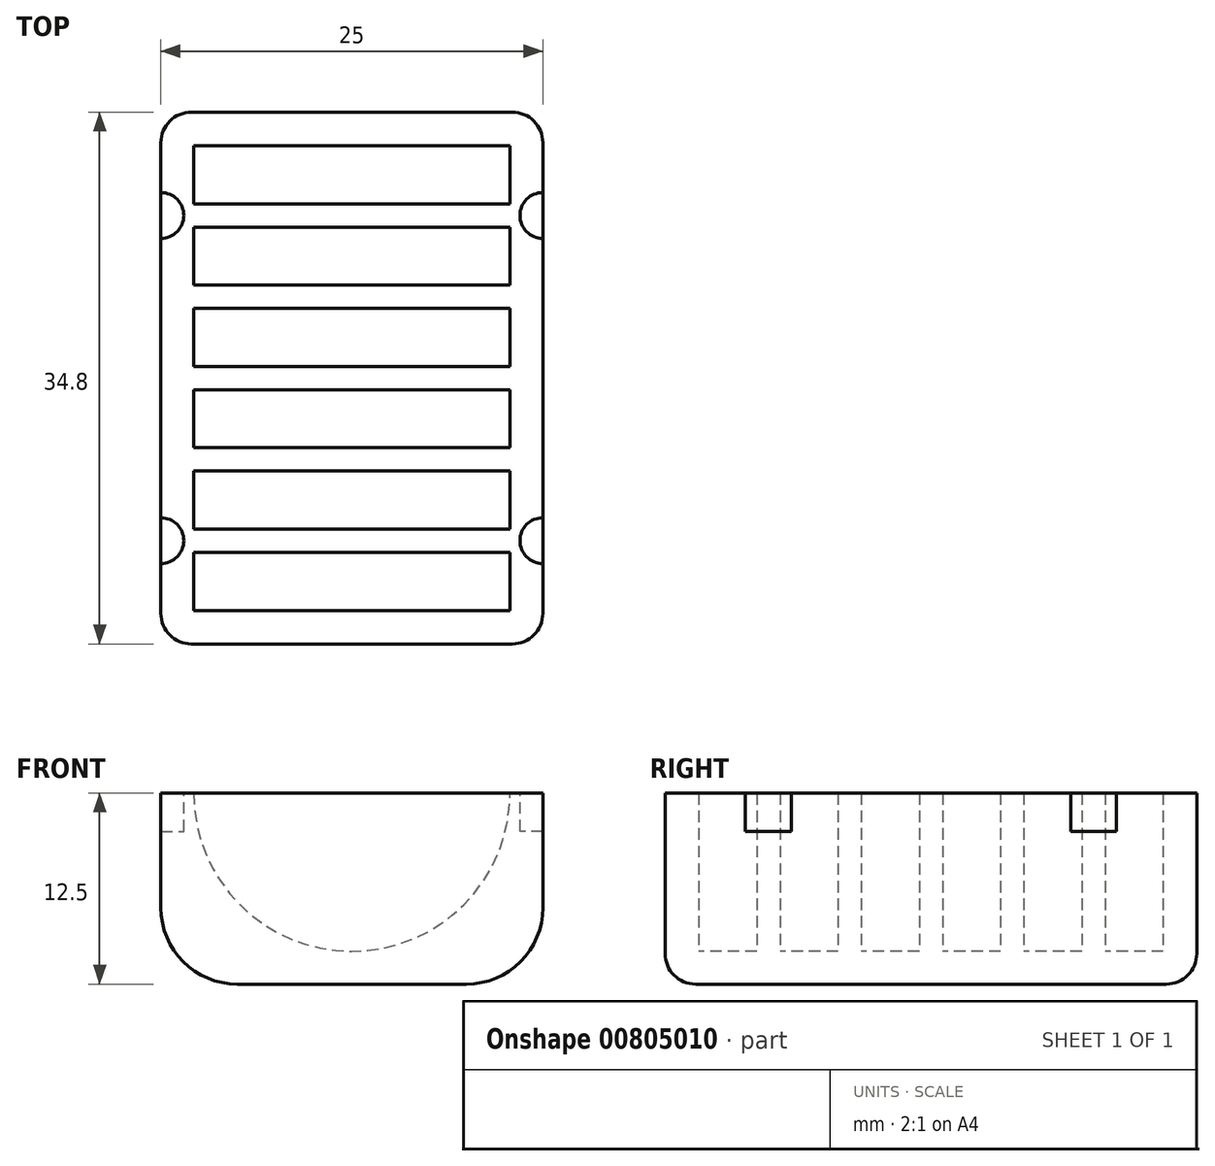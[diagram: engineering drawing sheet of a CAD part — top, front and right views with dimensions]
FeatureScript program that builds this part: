
annotation { "Feature Type Name" : "Feature", "Feature Type Description" : "" }
export const myFeature = defineFeature(function(context is Context, id is Id, definition is map)
    precondition{}
    {
        {
            var Q0;
            Q0=qCreatedBy(makeId("Top.planeOp"),FACE);
            var sketch = newSketch(context, id + "F0", { "sketchPlane" : qUnion([Q0])});
            skLineSegment(sketch, "E0.bottom", {"start": v(-30.1, 7.68) * mm, "end": v(-5.1, 7.68) * mm});
            skLineSegment(sketch, "E0.top", {"start": v(-30.1, -27.12) * mm, "end": v(-5.1, -27.12) * mm});
            skLineSegment(sketch, "E0.left", {"start": v(-30.1, 7.68) * mm, "end": v(-30.1, -27.12) * mm});
            skLineSegment(sketch, "E0.right", {"start": v(-5.1, 7.68) * mm, "end": v(-5.1, -27.12) * mm});
            skSolve(sketch);
        }
        {
            var Q0;
            Q0 = qSketchRegion(id + "F0", true);
            extrude(context, id + "F1", {"entities" : qUnion([Q0]), "depth" : (25 / 2) * mm, "offsetDistance" : 25 * mm});
        }
        {
            var Q0;
            Q0=makeQuery(id+"F1.opExtrude","SWEPT_FACE",FACE,{"disambiguationData":[OSD([sQuery(id+"F0.wireOp",EDGE,"E0.top")])]});
            var sketch = newSketch(context, id + "F2", { "sketchPlane" : qUnion([Q0])});
            skCircle(sketch, "E1", {"center": v(-17.6, 12.5) * mm, "radius": 10.35 * mm});
            skSolve(sketch);
        }
        {
            var Q0;
            Q0 = qSketchRegion(id + "F2", true);
            extrude(context, id + "F3", {"entities" : qUnion([Q0]), "operationType" : NewBodyOperationType.REMOVE, "oppositeDirection" : true, "depth" : (34.8 - 2.2) * mm, "offsetDistance" : 25 * mm, "hasSecondDirection" : true, "secondDirectionOppositeDirection" : true, "secondDirectionDepth" : (2.2) * mm});
        }
        {
            var Q0;
            Q0=makeQuery(id+"F1.opExtrude","CAP_FACE",FACE,{"disambiguationData":[OSD([sQuery(id+"F0.wireOp",EDGE,"E0.bottom"),sQuery(id+"F0.wireOp",EDGE,"E0.top"),sQuery(id+"F0.wireOp",EDGE,"E0.left"),sQuery(id+"F0.wireOp",EDGE,"E0.right")])],"isStart":false});
            var sketch = newSketch(context, id + "F4", { "sketchPlane" : qUnion([Q0])});
            skLineSegment(sketch, "E2.bottom", {"start": v(-27.95, 1.68) * mm, "end": v(-7.25, 1.68) * mm});
            skLineSegment(sketch, "E2.top", {"start": v(-27.95, 0.16) * mm, "end": v(-7.25, 0.16) * mm});
            skLineSegment(sketch, "E2.left", {"start": v(-27.95, 1.68) * mm, "end": v(-27.95, 0.16) * mm});
            skLineSegment(sketch, "E2.right", {"start": v(-7.25, 1.68) * mm, "end": v(-7.25, 0.16) * mm});
            skLineSegment(sketch, "E3.bottom", {"start": v(-27.95, -3.64) * mm, "end": v(-7.25, -3.64) * mm});
            skLineSegment(sketch, "E3.top", {"start": v(-27.95, -5.16) * mm, "end": v(-7.25, -5.16) * mm});
            skLineSegment(sketch, "E3.left", {"start": v(-27.95, -3.64) * mm, "end": v(-27.95, -5.16) * mm});
            skLineSegment(sketch, "E3.right", {"start": v(-7.25, -3.64) * mm, "end": v(-7.25, -5.16) * mm});
            skLineSegment(sketch, "E4.bottom", {"start": v(-27.95, -8.96) * mm, "end": v(-7.25, -8.96) * mm});
            skLineSegment(sketch, "E4.top", {"start": v(-27.95, -10.48) * mm, "end": v(-7.25, -10.48) * mm});
            skLineSegment(sketch, "E4.left", {"start": v(-27.95, -8.96) * mm, "end": v(-27.95, -10.48) * mm});
            skLineSegment(sketch, "E4.right", {"start": v(-7.25, -8.96) * mm, "end": v(-7.25, -10.48) * mm});
            skLineSegment(sketch, "E5.bottom", {"start": v(-27.95, -14.28) * mm, "end": v(-7.25, -14.28) * mm});
            skLineSegment(sketch, "E5.top", {"start": v(-27.95, -15.8) * mm, "end": v(-7.25, -15.8) * mm});
            skLineSegment(sketch, "E5.left", {"start": v(-27.95, -14.28) * mm, "end": v(-27.95, -15.8) * mm});
            skLineSegment(sketch, "E5.right", {"start": v(-7.25, -14.28) * mm, "end": v(-7.25, -15.8) * mm});
            skLineSegment(sketch, "E6.top", {"start": v(-27.95, -21.12) * mm, "end": v(-7.25, -21.12) * mm});
            skLineSegment(sketch, "E7", {"start": v(-27.95, -21.12) * mm, "end": v(-27.95, -19.6) * mm});
            skLineSegment(sketch, "E8", {"start": v(-27.95, -19.6) * mm, "end": v(-7.25, -19.6) * mm});
            skLineSegment(sketch, "E9", {"start": v(-7.25, -19.6) * mm, "end": v(-7.25, -21.12) * mm});
            skSolve(sketch);
        }
        {
            var Q0;
            Q0 = qSketchRegion(id + "F4", true);
            extrude(context, id + "F5", {"entities" : qUnion([Q0]), "operationType" : NewBodyOperationType.ADD, "oppositeDirection" : true, "depth" : 10.6 * mm, "offsetDistance" : 25 * mm});
        }
        {
            var Q0;
            Q0=makeQuery(id+"F1.opExtrude","CAP_EDGE",EDGE,{"disambiguationData":[OSD([sQuery(id+"F0.wireOp",EDGE,"E0.right")])],"isStart":true});
            var Q1;
            Q1=makeQuery(id+"F1.opExtrude","CAP_EDGE",EDGE,{"disambiguationData":[OSD([sQuery(id+"F0.wireOp",EDGE,"E0.left")])],"isStart":true});
            fillet(context, id + "F6", {"entities" : qUnion([Q0, Q1]), "radius" : 5 * mm, "tangentPropagation" : true, "allowEdgeOverflow" : false});
        }
        {
            var Q0;
            Q0=makeQuery(id+"F1.opExtrude","SWEPT_EDGE",EDGE,{"disambiguationData":[OSD([sQuery(id+"F0.wireOp",EDGE,"E0.top"),sQuery(id+"F0.wireOp",EDGE,"E0.right")])]});
            var Q1;
            Q1=makeQuery(id+"F1.opExtrude","SWEPT_EDGE",EDGE,{"disambiguationData":[OSD([sQuery(id+"F0.wireOp",EDGE,"E0.bottom"),sQuery(id+"F0.wireOp",EDGE,"E0.right")])]});
            fillet(context, id + "F7", {"entities" : qUnion([Q0, Q1]), "radius" : 2 * mm, "tangentPropagation" : true, "allowEdgeOverflow" : false});
        }
        {
            var Q0;
            Q0=makeQuery(id+"F5.boolean.opBoolean","MERGE",FACE,{"derivedFrom":[makeQuery(id+"F1.opExtrude","CAP_FACE",FACE,{"disambiguationData":[OSD([sQuery(id+"F0.wireOp",EDGE,"E0.bottom"),sQuery(id+"F0.wireOp",EDGE,"E0.top"),sQuery(id+"F0.wireOp",EDGE,"E0.left"),sQuery(id+"F0.wireOp",EDGE,"E0.right")])],"isStart":false}),makeQuery(id+"F5.opExtrude","CAP_FACE",FACE,{"disambiguationData":[OSD([sQuery(id+"F4.wireOp",EDGE,"E2.bottom"),sQuery(id+"F4.wireOp",EDGE,"E2.top"),sQuery(id+"F4.wireOp",EDGE,"E2.left"),sQuery(id+"F4.wireOp",EDGE,"E2.right")])],"isStart":true}),makeQuery(id+"F5.opExtrude","CAP_FACE",FACE,{"disambiguationData":[OSD([sQuery(id+"F4.wireOp",EDGE,"E3.bottom"),sQuery(id+"F4.wireOp",EDGE,"E3.top"),sQuery(id+"F4.wireOp",EDGE,"E3.left"),sQuery(id+"F4.wireOp",EDGE,"E3.right")])],"isStart":true}),makeQuery(id+"F5.opExtrude","CAP_FACE",FACE,{"disambiguationData":[OSD([sQuery(id+"F4.wireOp",EDGE,"E4.bottom"),sQuery(id+"F4.wireOp",EDGE,"E4.top"),sQuery(id+"F4.wireOp",EDGE,"E4.left"),sQuery(id+"F4.wireOp",EDGE,"E4.right")])],"isStart":true}),makeQuery(id+"F5.opExtrude","CAP_FACE",FACE,{"disambiguationData":[OSD([sQuery(id+"F4.wireOp",EDGE,"E5.bottom"),sQuery(id+"F4.wireOp",EDGE,"E5.top"),sQuery(id+"F4.wireOp",EDGE,"E5.left"),sQuery(id+"F4.wireOp",EDGE,"E5.right")])],"isStart":true}),makeQuery(id+"F5.opExtrude","CAP_FACE",FACE,{"disambiguationData":[OSD([sQuery(id+"F4.wireOp",EDGE,"E6.top"),sQuery(id+"F4.wireOp",EDGE,"E7"),sQuery(id+"F4.wireOp",EDGE,"E8"),sQuery(id+"F4.wireOp",EDGE,"E9")])],"isStart":true})]});
            var sketch = newSketch(context, id + "F8", { "sketchPlane" : qUnion([Q0])});
            skCircle(sketch, "E10", {"center": v(-30.1, 0.92) * mm, "radius": 1.5 * mm});
            skCircle(sketch, "E11.1.0.0", {"center": v(-5.1, 0.92) * mm, "radius": 1.5 * mm});
            skCircle(sketch, "E12.MirrorC", {"center": v(-5.1, -20.36) * mm, "radius": 1.5 * mm});
            skCircle(sketch, "E13.MirrorC", {"center": v(-30.1, -20.36) * mm, "radius": 1.5 * mm});
            skSolve(sketch);
        }
        {
            var Q0;
            Q0 = qSketchRegion(id + "F8", true);
            extrude(context, id + "F9", {"entities" : qUnion([Q0]), "operationType" : NewBodyOperationType.REMOVE, "oppositeDirection" : true, "depth" : 2.5 * mm, "offsetDistance" : 25 * mm});
        }
    });
